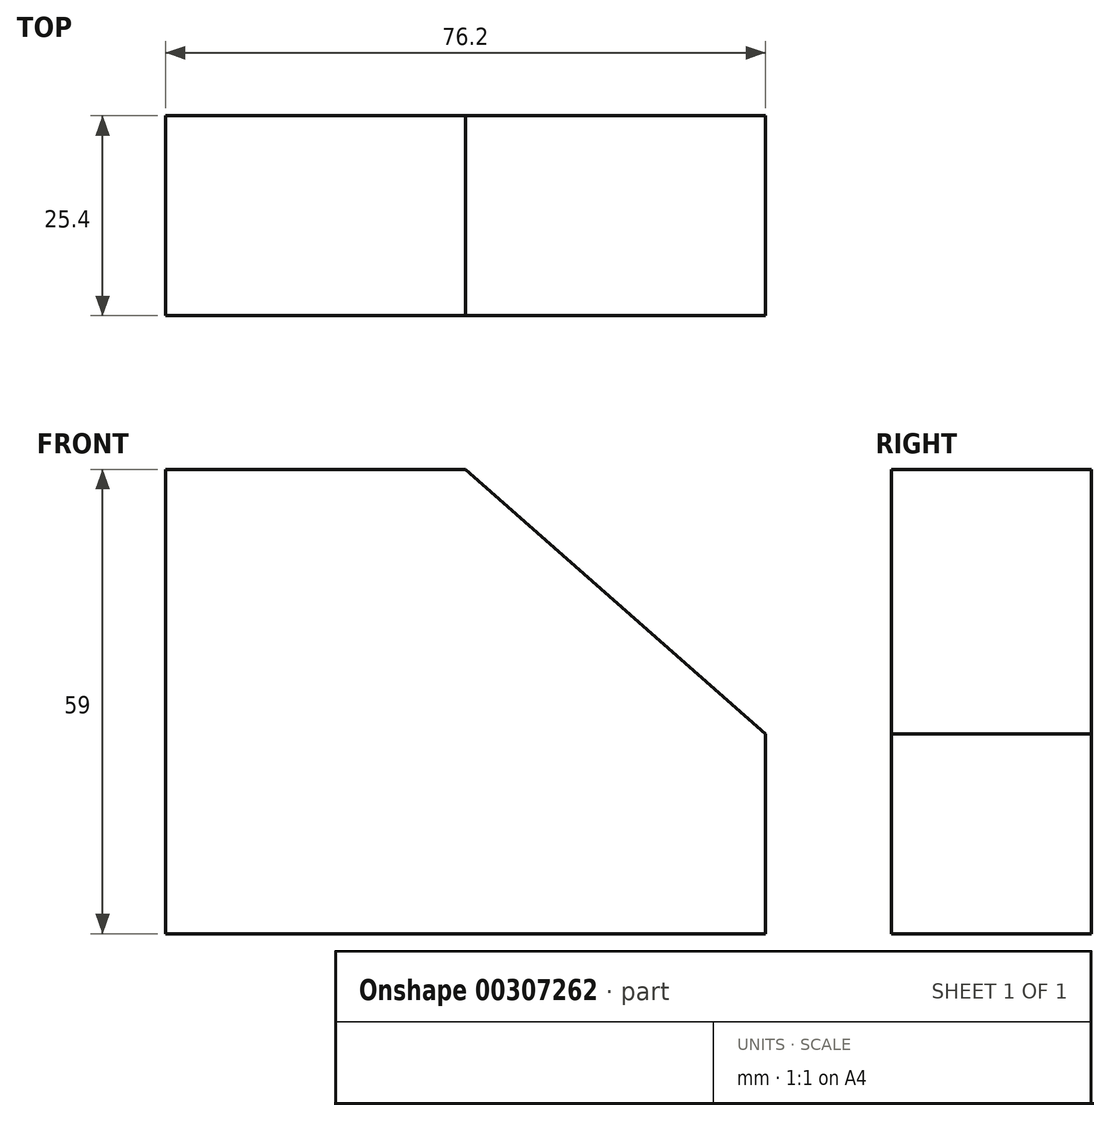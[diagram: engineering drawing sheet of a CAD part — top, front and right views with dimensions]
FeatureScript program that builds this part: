
annotation { "Feature Type Name" : "Feature", "Feature Type Description" : "" }
export const myFeature = defineFeature(function(context is Context, id is Id, definition is map)
    precondition{}
    {
        {
            var Q0;
            Q0=qCreatedBy(makeId("Front.planeOp"),FACE);
            var sketch = newSketch(context, id + "F0", { "sketchPlane" : qUnion([Q0])});
            skLineSegment(sketch, "E0", {"start": v(-28.68, -36.73) * mm, "end": v(47.52, -36.73) * mm});
            skLineSegment(sketch, "E1", {"start": v(47.52, -36.73) * mm, "end": v(47.52, -11.33) * mm});
            skLineSegment(sketch, "E2", {"start": v(47.52, -11.33) * mm, "end": v(9.42, 22.27) * mm});
            skLineSegment(sketch, "E3", {"start": v(9.42, 22.27) * mm, "end": v(-28.68, 22.27) * mm});
            skLineSegment(sketch, "E4", {"start": v(-28.68, 22.27) * mm, "end": v(-28.68, -36.73) * mm});
            skSolve(sketch);
        }
        {
            var Q0;
            Q0=makeQuery(id+"F0.imprint","IMPRINT",FACE,{"disambiguationData":[TD([[makeQuery(id+"F0.imprint","IMPRINT",EDGE,{"derivedFrom":sQuery(id+"F0.wireOp",EDGE,"E0")}),1.0]])]});
            extrude(context, id + "F1", {"entities" : qUnion([Q0]), "depth" : 25.4 * mm});
        }
    });
